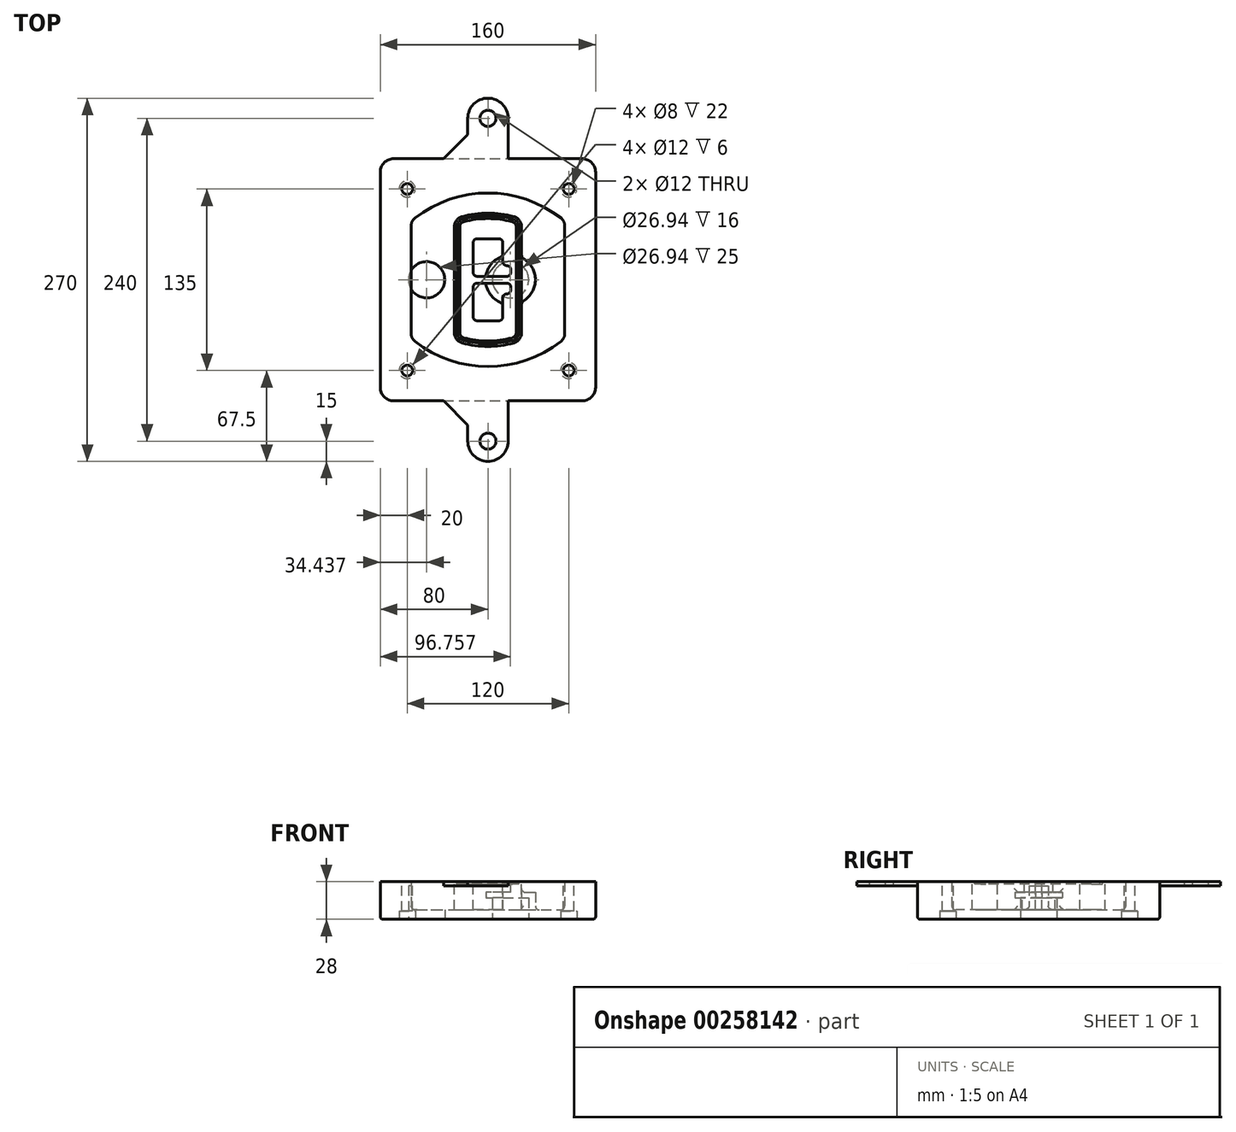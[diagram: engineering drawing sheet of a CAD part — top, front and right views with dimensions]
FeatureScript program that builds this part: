
annotation { "Feature Type Name" : "Feature", "Feature Type Description" : "" }
export const myFeature = defineFeature(function(context is Context, id is Id, definition is map)
    precondition{}
    {
        {
            var Q0;
            Q0=qCreatedBy(makeId("Top.planeOp"),FACE);
            var sketch = newSketch(context, id + "F0", { "sketchPlane" : qUnion([Q0])});
            skPoint(sketch, "E0.rect.middle", {"position": v(0, 0) * mm});
            skLineSegment(sketch, "E1.bottom", {"start": v(-70, -90) * mm, "end": v(70, -90) * mm});
            skLineSegment(sketch, "E1.top", {"start": v(-70, 90) * mm, "end": v(70, 90) * mm});
            skLineSegment(sketch, "E1.left", {"start": v(-80, -80) * mm, "end": v(-80, 80) * mm});
            skLineSegment(sketch, "E1.right", {"start": v(80, -80) * mm, "end": v(80, 80) * mm});
            skLineSegment(sketch, "E2", {"start": v(-80, 90) * mm, "end": v(80, -90) * mm, "construction": true});
            skLineSegment(sketch, "E3", {"start": v(80, 90) * mm, "end": v(-80, -90) * mm, "construction": true});
            skCircle(sketch, "E4", {"center": v(-60, 67.5) * mm, "radius": 4 * mm});
            skCircle(sketch, "E5", {"center": v(60, 67.5) * mm, "radius": 4 * mm});
            skCircle(sketch, "E6", {"center": v(60, -67.5) * mm, "radius": 4 * mm});
            skCircle(sketch, "E7", {"center": v(-60, -67.5) * mm, "radius": 4 * mm});
            skLineSegment(sketch, "E8", {"start": v(-60, 67.5) * mm, "end": v(60, 67.5) * mm, "construction": true});
            skLineSegment(sketch, "E9", {"start": v(60, 67.5) * mm, "end": v(60, -67.5) * mm, "construction": true});
            skLineSegment(sketch, "E10", {"start": v(60, -67.5) * mm, "end": v(-60, -67.5) * mm, "construction": true});
            skLineSegment(sketch, "E11", {"start": v(-60, -67.5) * mm, "end": v(-60, 67.5) * mm, "construction": true});
            skLineSegment(sketch, "E12", {"start": v(-60, 40.3) * mm, "end": v(-60, -40.3) * mm});
            skLineSegment(sketch, "E13", {"start": v(60, 40.3) * mm, "end": v(60, -40.3) * mm});
            skArc(sketch, "E14", {"start": v(56.15, 48.18) * mm, "mid": v(0, 67.5) * mm, "end": v(-56.15, 48.18) * mm});
            skArc(sketch, "E15", {"start": v(-56.15, -48.18) * mm, "mid": v(0, -67.5) * mm, "end": v(56.15, -48.18) * mm});
            skLineSegment(sketch, "E16", {"start": v(-60, 0) * mm, "end": v(60, 0) * mm, "construction": true});
            skPoint(sketch, "E17.visualSharp", {"position": v(-60, -45) * mm});
            skArc(sketch, "E17.filletArc", {"start": v(-60, -40.3) * mm, "mid": v(-58.99, -44.68) * mm, "end": v(-56.15, -48.18) * mm});
            skPoint(sketch, "E18.visualSharp", {"position": v(-60, 45) * mm});
            skArc(sketch, "E18.filletArc", {"start": v(-56.15, 48.18) * mm, "mid": v(-58.99, 44.68) * mm, "end": v(-60, 40.3) * mm});
            skPoint(sketch, "E19.visualSharp", {"position": v(60, 45) * mm});
            skArc(sketch, "E19.filletArc", {"start": v(60, 40.3) * mm, "mid": v(58.99, 44.68) * mm, "end": v(56.15, 48.18) * mm});
            skPoint(sketch, "E20.visualSharp", {"position": v(60, -45) * mm});
            skArc(sketch, "E20.filletArc", {"start": v(56.15, -48.18) * mm, "mid": v(58.99, -44.68) * mm, "end": v(60, -40.3) * mm});
            skPoint(sketch, "E21.visualSharp", {"position": v(-80, 90) * mm});
            skArc(sketch, "E21.filletArc", {"start": v(-70, 90) * mm, "mid": v(-77.07, 87.07) * mm, "end": v(-80, 80) * mm});
            skPoint(sketch, "E22.visualSharp", {"position": v(80, 90) * mm});
            skArc(sketch, "E22.filletArc", {"start": v(80, 80) * mm, "mid": v(77.07, 87.07) * mm, "end": v(70, 90) * mm});
            skPoint(sketch, "E23.visualSharp", {"position": v(80, -90) * mm});
            skArc(sketch, "E23.filletArc", {"start": v(70, -90) * mm, "mid": v(77.07, -87.07) * mm, "end": v(80, -80) * mm});
            skPoint(sketch, "E24.visualSharp", {"position": v(-80, -90) * mm});
            skArc(sketch, "E24.filletArc", {"start": v(-80, -80) * mm, "mid": v(-77.07, -87.07) * mm, "end": v(-70, -90) * mm});
            skArc(sketch, "E25.0", {"start": v(57, 40.3) * mm, "mid": v(56.3, 43.36) * mm, "end": v(54.3, 45.81) * mm});
            skLineSegment(sketch, "E25.1", {"start": v(57, 40.3) * mm, "end": v(57, -40.3) * mm});
            skArc(sketch, "E25.2", {"start": v(54.3, -45.81) * mm, "mid": v(56.3, -43.36) * mm, "end": v(57, -40.3) * mm});
            skArc(sketch, "E25.3", {"start": v(-54.3, -45.81) * mm, "mid": v(0, -64.5) * mm, "end": v(54.3, -45.81) * mm});
            skArc(sketch, "E25.4", {"start": v(-57, -40.3) * mm, "mid": v(-56.3, -43.36) * mm, "end": v(-54.3, -45.81) * mm});
            skArc(sketch, "E25.5", {"start": v(54.3, 45.81) * mm, "mid": v(0, 64.5) * mm, "end": v(-54.3, 45.81) * mm});
            skLineSegment(sketch, "E25.6", {"start": v(-57, 40.3) * mm, "end": v(-57, -40.3) * mm});
            skArc(sketch, "E25.7", {"start": v(-54.3, 45.81) * mm, "mid": v(-56.3, 43.36) * mm, "end": v(-57, 40.3) * mm});
            skArc(sketch, "E26.0", {"start": v(-58.62, 51.33) * mm, "mid": v(-62.58, 46.43) * mm, "end": v(-64, 40.3) * mm});
            skArc(sketch, "E26.1", {"start": v(58.62, 51.33) * mm, "mid": v(0, 71.5) * mm, "end": v(-58.62, 51.33) * mm});
            skArc(sketch, "E26.2", {"start": v(64, 40.3) * mm, "mid": v(62.58, 46.43) * mm, "end": v(58.62, 51.33) * mm});
            skLineSegment(sketch, "E26.3", {"start": v(64, 40.3) * mm, "end": v(64, -40.3) * mm});
            skArc(sketch, "E26.4", {"start": v(58.62, -51.33) * mm, "mid": v(62.58, -46.43) * mm, "end": v(64, -40.3) * mm});
            skLineSegment(sketch, "E26.5", {"start": v(-64, 40.3) * mm, "end": v(-64, -40.3) * mm});
            skArc(sketch, "E26.6", {"start": v(-58.62, -51.33) * mm, "mid": v(0, -71.5) * mm, "end": v(58.62, -51.33) * mm});
            skArc(sketch, "E26.7", {"start": v(-64, -40.3) * mm, "mid": v(-62.58, -46.43) * mm, "end": v(-58.62, -51.33) * mm});
            skSolve(sketch);
        }
        {
            var Q0;
            Q0=makeQuery(id+"F0.imprint","IMPRINT",FACE,{"disambiguationData":[TD([[makeQuery(id+"F0.imprint","IMPRINT",EDGE,{"derivedFrom":sQuery(id+"F0.wireOp",EDGE,"E1.bottom")}),1.0]])]});
            var Q1;
            Q1=makeQuery(id+"F0.imprint","IMPRINT",FACE,{"disambiguationData":[TD([[makeQuery(id+"F0.imprint","IMPRINT",EDGE,{"derivedFrom":sQuery(id+"F0.wireOp",EDGE,"E12")}),1.0]])]});
            var Q2;
            Q2=makeQuery(id+"F0.imprint","IMPRINT",FACE,{"disambiguationData":[TD([[makeQuery(id+"F0.imprint","IMPRINT",EDGE,{"derivedFrom":sQuery(id+"F0.wireOp",EDGE,"E25.0")}),1.0]])]});
            var Q3;
            Q3=makeQuery(id+"F0.imprint","IMPRINT",FACE,{"disambiguationData":[TD([[makeQuery(id+"F0.imprint","IMPRINT",EDGE,{"derivedFrom":sQuery(id+"F0.wireOp",EDGE,"E12")}),-1.0]])]});
            extrude(context, id + "F1", {"entities" : qUnion([Q0, Q1, Q2, Q3]), "oppositeDirection" : true, "depth" : 25 * mm});
        }
        {
            var Q0;
            Q0=makeQuery(id+"F0.imprint","IMPRINT",FACE,{"disambiguationData":[TD([[makeQuery(id+"F0.imprint","IMPRINT",EDGE,{"derivedFrom":sQuery(id+"F0.wireOp",EDGE,"E12")}),1.0]])]});
            extrude(context, id + "F2", {"entities" : qUnion([Q0]), "operationType" : NewBodyOperationType.ADD, "depth" : 3 * mm});
        }
        {
            var Q0;
            Q0=makeQuery(id+"F0.imprint","IMPRINT",FACE,{"disambiguationData":[TD([[makeQuery(id+"F0.imprint","IMPRINT",EDGE,{"derivedFrom":sQuery(id+"F0.wireOp",EDGE,"E25.0")}),1.0]])]});
            extrude(context, id + "F3", {"entities" : qUnion([Q0]), "operationType" : NewBodyOperationType.REMOVE, "oppositeDirection" : true, "depth" : 18 * mm});
        }
        {
            var Q0;
            Q0=makeQuery(id+"F2.opExtrude","CAP_FACE",FACE,{"disambiguationData":[OSD([sQuery(id+"F0.wireOp",EDGE,"E12"),sQuery(id+"F0.wireOp",EDGE,"E13"),sQuery(id+"F0.wireOp",EDGE,"E14"),sQuery(id+"F0.wireOp",EDGE,"E15"),sQuery(id+"F0.wireOp",EDGE,"E17.filletArc"),sQuery(id+"F0.wireOp",EDGE,"E18.filletArc"),sQuery(id+"F0.wireOp",EDGE,"E19.filletArc"),sQuery(id+"F0.wireOp",EDGE,"E20.filletArc"),sQuery(id+"F0.wireOp",EDGE,"E25.0"),sQuery(id+"F0.wireOp",EDGE,"E25.1"),sQuery(id+"F0.wireOp",EDGE,"E25.2"),sQuery(id+"F0.wireOp",EDGE,"E25.3"),sQuery(id+"F0.wireOp",EDGE,"E25.4"),sQuery(id+"F0.wireOp",EDGE,"E25.5"),sQuery(id+"F0.wireOp",EDGE,"E25.6"),sQuery(id+"F0.wireOp",EDGE,"E25.7")])],"isStart":false});
            var sketch = newSketch(context, id + "F4", { "sketchPlane" : qUnion([Q0])});
            skArc(sketch, "E27.0", {"start": v(-19.08, -46.97) * mm, "mid": v(0, -49.5) * mm, "end": v(19.08, -46.97) * mm});
            skArc(sketch, "E28.0", {"start": v(19.08, 46.97) * mm, "mid": v(0, 49.5) * mm, "end": v(-19.08, 46.97) * mm});
            skLineSegment(sketch, "E29", {"start": v(-25, 39.25) * mm, "end": v(-25, -39.25) * mm});
            skLineSegment(sketch, "E30", {"start": v(25, 39.25) * mm, "end": v(25, -39.25) * mm});
            skLineSegment(sketch, "E31", {"start": v(-25, 45.1) * mm, "end": v(25, 45.1) * mm, "construction": true});
            skLineSegment(sketch, "E32", {"start": v(-25, -45.1) * mm, "end": v(25, -45.1) * mm, "construction": true});
            skPoint(sketch, "E33.visualSharp", {"position": v(-25, 45.1) * mm});
            skArc(sketch, "E33.filletArc", {"start": v(-19.08, 46.97) * mm, "mid": v(-23.35, 44.11) * mm, "end": v(-25, 39.25) * mm});
            skPoint(sketch, "E34.visualSharp", {"position": v(25, 45.1) * mm});
            skArc(sketch, "E34.filletArc", {"start": v(25, 39.25) * mm, "mid": v(23.35, 44.11) * mm, "end": v(19.08, 46.97) * mm});
            skPoint(sketch, "E35.visualSharp", {"position": v(25, -45.1) * mm});
            skArc(sketch, "E35.filletArc", {"start": v(19.08, -46.97) * mm, "mid": v(23.35, -44.11) * mm, "end": v(25, -39.25) * mm});
            skPoint(sketch, "E36.visualSharp", {"position": v(-25, -45.1) * mm});
            skArc(sketch, "E36.filletArc", {"start": v(-25, -39.25) * mm, "mid": v(-23.35, -44.11) * mm, "end": v(-19.08, -46.97) * mm});
            skArc(sketch, "E37.0", {"start": v(54.3, 45.81) * mm, "mid": v(0, 64.5) * mm, "end": v(-54.3, 45.81) * mm});
            skArc(sketch, "E37.1", {"start": v(-54.3, 45.81) * mm, "mid": v(-56.3, 43.36) * mm, "end": v(-57, 40.3) * mm});
            skLineSegment(sketch, "E37.2", {"start": v(-57, 40.3) * mm, "end": v(-57, -40.3) * mm});
            skArc(sketch, "E37.3", {"start": v(-57, -40.3) * mm, "mid": v(-56.3, -43.36) * mm, "end": v(-54.3, -45.81) * mm});
            skArc(sketch, "E37.4", {"start": v(-54.3, -45.81) * mm, "mid": v(0, -64.5) * mm, "end": v(54.3, -45.81) * mm});
            skArc(sketch, "E37.5", {"start": v(54.3, -45.81) * mm, "mid": v(56.3, -43.36) * mm, "end": v(57, -40.3) * mm});
            skLineSegment(sketch, "E37.6", {"start": v(57, 40.3) * mm, "end": v(57, -40.3) * mm});
            skArc(sketch, "E37.7", {"start": v(57, 40.3) * mm, "mid": v(56.3, 43.36) * mm, "end": v(54.3, 45.81) * mm});
            skLineSegment(sketch, "E38.0", {"start": v(23, 39.25) * mm, "end": v(23, -39.25) * mm});
            skArc(sketch, "E38.1", {"start": v(18.56, -45.04) * mm, "mid": v(21.76, -42.9) * mm, "end": v(23, -39.25) * mm});
            skArc(sketch, "E38.2", {"start": v(-18.56, -45.04) * mm, "mid": v(0, -47.5) * mm, "end": v(18.56, -45.04) * mm});
            skArc(sketch, "E38.3", {"start": v(-23, -39.25) * mm, "mid": v(-21.76, -42.9) * mm, "end": v(-18.56, -45.04) * mm});
            skLineSegment(sketch, "E38.4", {"start": v(-23, 39.25) * mm, "end": v(-23, -39.25) * mm});
            skArc(sketch, "E38.5", {"start": v(23, 39.25) * mm, "mid": v(21.76, 42.9) * mm, "end": v(18.56, 45.04) * mm});
            skArc(sketch, "E38.6", {"start": v(-18.56, 45.04) * mm, "mid": v(-21.76, 42.9) * mm, "end": v(-23, 39.25) * mm});
            skArc(sketch, "E38.7", {"start": v(18.56, 45.04) * mm, "mid": v(0, 47.5) * mm, "end": v(-18.56, 45.04) * mm});
            skArc(sketch, "E39.0", {"start": v(21, 39.25) * mm, "mid": v(20.18, 41.68) * mm, "end": v(18.04, 43.1) * mm});
            skLineSegment(sketch, "E39.1", {"start": v(21, 39.25) * mm, "end": v(21, -39.25) * mm});
            skArc(sketch, "E39.2", {"start": v(18.04, -43.1) * mm, "mid": v(20.18, -41.68) * mm, "end": v(21, -39.25) * mm});
            skArc(sketch, "E39.3", {"start": v(-18.04, -43.1) * mm, "mid": v(0, -45.5) * mm, "end": v(18.04, -43.1) * mm});
            skArc(sketch, "E39.4", {"start": v(-21, -39.25) * mm, "mid": v(-20.18, -41.68) * mm, "end": v(-18.04, -43.1) * mm});
            skArc(sketch, "E39.5", {"start": v(18.04, 43.1) * mm, "mid": v(0, 45.5) * mm, "end": v(-18.04, 43.1) * mm});
            skLineSegment(sketch, "E39.6", {"start": v(-21, 39.25) * mm, "end": v(-21, -39.25) * mm});
            skArc(sketch, "E39.7", {"start": v(-18.04, 43.1) * mm, "mid": v(-20.18, 41.68) * mm, "end": v(-21, 39.25) * mm});
            skLineSegment(sketch, "E40", {"start": v(-25, 0) * mm, "end": v(25, 0) * mm, "construction": true});
            skLineSegment(sketch, "E41", {"start": v(-11, 5.5) * mm, "end": v(-11, 27.5) * mm});
            skLineSegment(sketch, "E42", {"start": v(-8, 30.5) * mm, "end": v(8, 30.5) * mm});
            skLineSegment(sketch, "E43", {"start": v(11, 27.5) * mm, "end": v(11, 13.5) * mm});
            skLineSegment(sketch, "E44", {"start": v(14, 10.5) * mm, "end": v(14, 10.5) * mm});
            skLineSegment(sketch, "E45", {"start": v(17, 7.5) * mm, "end": v(17, 5.5) * mm});
            skLineSegment(sketch, "E46", {"start": v(14, 2.5) * mm, "end": v(-8, 2.5) * mm});
            skPoint(sketch, "E47.visualSharp", {"position": v(-11, 30.5) * mm});
            skArc(sketch, "E47.filletArc", {"start": v(-8, 30.5) * mm, "mid": v(-10.12, 29.62) * mm, "end": v(-11, 27.5) * mm});
            skPoint(sketch, "E48.visualSharp", {"position": v(11, 30.5) * mm});
            skArc(sketch, "E48.filletArc", {"start": v(11, 27.5) * mm, "mid": v(10.12, 29.62) * mm, "end": v(8, 30.5) * mm});
            skPoint(sketch, "E49.visualSharp", {"position": v(11, 10.5) * mm});
            skArc(sketch, "E49.filletArc", {"start": v(11, 13.5) * mm, "mid": v(11.88, 11.38) * mm, "end": v(14, 10.5) * mm});
            skPoint(sketch, "E50.visualSharp", {"position": v(17, 10.5) * mm});
            skArc(sketch, "E50.filletArc", {"start": v(17, 7.5) * mm, "mid": v(16.12, 9.62) * mm, "end": v(14, 10.5) * mm});
            skPoint(sketch, "E51.visualSharp", {"position": v(17, 2.5) * mm});
            skArc(sketch, "E51.filletArc", {"start": v(14, 2.5) * mm, "mid": v(16.12, 3.38) * mm, "end": v(17, 5.5) * mm});
            skPoint(sketch, "E52.visualSharp", {"position": v(-11, 2.5) * mm});
            skArc(sketch, "E52.filletArc", {"start": v(-11, 5.5) * mm, "mid": v(-10.12, 3.38) * mm, "end": v(-8, 2.5) * mm});
            skLineSegment(sketch, "E53.0.MirrorCS", {"start": v(14, -2.5) * mm, "end": v(-8, -2.5) * mm});
            skArc(sketch, "E54.0.MirrorCS", {"start": v(-11, -5.5) * mm, "mid": v(-10.12, -3.38) * mm, "end": v(-8, -2.5) * mm});
            skLineSegment(sketch, "E55.0.MirrorCS", {"start": v(-11, -5.5) * mm, "end": v(-11, -27.5) * mm});
            skArc(sketch, "E56.0.MirrorCS", {"start": v(-8, -30.5) * mm, "mid": v(-10.12, -29.62) * mm, "end": v(-11, -27.5) * mm});
            skLineSegment(sketch, "E57.0.MirrorCS", {"start": v(-8, -30.5) * mm, "end": v(8, -30.5) * mm});
            skArc(sketch, "E58.0.MirrorCS", {"start": v(11, -27.5) * mm, "mid": v(10.12, -29.62) * mm, "end": v(8, -30.5) * mm});
            skLineSegment(sketch, "E59.0.MirrorCS", {"start": v(11, -27.5) * mm, "end": v(11, -13.5) * mm});
            skArc(sketch, "E60.0.MirrorCS", {"start": v(11, -13.5) * mm, "mid": v(11.88, -11.38) * mm, "end": v(14, -10.5) * mm});
            skArc(sketch, "E61.0.MirrorCS", {"start": v(17, -7.5) * mm, "mid": v(16.12, -9.62) * mm, "end": v(14, -10.5) * mm});
            skLineSegment(sketch, "E62.0.MirrorCS", {"start": v(17, -7.5) * mm, "end": v(17, -5.5) * mm});
            skArc(sketch, "E63.0.MirrorCS", {"start": v(14, -2.5) * mm, "mid": v(16.12, -3.38) * mm, "end": v(17, -5.5) * mm});
            skSolve(sketch);
        }
        {
            var Q0;
            Q0=makeQuery(id+"F4.imprint","IMPRINT",FACE,{"disambiguationData":[TD([[makeQuery(id+"F4.imprint","IMPRINT",EDGE,{"derivedFrom":sQuery(id+"F4.wireOp",EDGE,"E27.0")}),1.0]])]});
            var Q1;
            Q1=makeQuery(id+"F4.imprint","IMPRINT",FACE,{"disambiguationData":[TD([[makeQuery(id+"F4.imprint","IMPRINT",EDGE,{"derivedFrom":sQuery(id+"F4.wireOp",EDGE,"E38.0")}),-1.0]])]});
            var Q2;
            Q2=makeQuery(id+"F4.imprint","IMPRINT",FACE,{"disambiguationData":[TD([[makeQuery(id+"F4.imprint","IMPRINT",EDGE,{"derivedFrom":sQuery(id+"F4.wireOp",EDGE,"E39.0")}),1.0]])]});
            extrude(context, id + "F5", {"entities" : qUnion([Q0, Q1, Q2]), "operationType" : NewBodyOperationType.ADD, "endBound" : BoundingType.UP_TO_NEXT, "oppositeDirection" : true, "depth" : 25 * mm});
        }
        {
            var Q0;
            Q0=makeQuery(id+"F4.imprint","IMPRINT",FACE,{"disambiguationData":[TD([[makeQuery(id+"F4.imprint","IMPRINT",EDGE,{"derivedFrom":sQuery(id+"F4.wireOp",EDGE,"E38.0")}),-1.0]])]});
            extrude(context, id + "F6", {"entities" : qUnion([Q0]), "operationType" : NewBodyOperationType.REMOVE, "oppositeDirection" : true, "depth" : 2 * mm});
        }
        {
            var Q0;
            Q0=makeQuery(id+"F1.opExtrude","CAP_FACE",FACE,{"disambiguationData":[OSD([sQuery(id+"F0.wireOp",EDGE,"E1.bottom"),sQuery(id+"F0.wireOp",EDGE,"E1.top"),sQuery(id+"F0.wireOp",EDGE,"E1.left"),sQuery(id+"F0.wireOp",EDGE,"E1.right"),sQuery(id+"F0.wireOp",EDGE,"E4"),sQuery(id+"F0.wireOp",EDGE,"E5"),sQuery(id+"F0.wireOp",EDGE,"E6"),sQuery(id+"F0.wireOp",EDGE,"E7"),sQuery(id+"F0.wireOp",EDGE,"E21.filletArc"),sQuery(id+"F0.wireOp",EDGE,"E22.filletArc"),sQuery(id+"F0.wireOp",EDGE,"E23.filletArc"),sQuery(id+"F0.wireOp",EDGE,"E24.filletArc")])],"isStart":false});
            var sketch = newSketch(context, id + "F7", { "sketchPlane" : qUnion([Q0])});
            skCircle(sketch, "E64", {"center": v(16.76, 0) * mm, "radius": 13.47 * mm});
            skCircle(sketch, "E65", {"center": v(-45.56, 0) * mm, "radius": 13.47 * mm});
            skLineSegment(sketch, "E66", {"start": v(80, 0) * mm, "end": v(-80, 0) * mm});
            skCircle(sketch, "E67", {"center": v(16.76, 0) * mm, "radius": 18.47 * mm});
            skCircle(sketch, "E68", {"center": v(60, -67.5) * mm, "radius": 6 * mm});
            skCircle(sketch, "E69", {"center": v(-60, -67.5) * mm, "radius": 6 * mm});
            skCircle(sketch, "E70", {"center": v(-60, 67.5) * mm, "radius": 6 * mm});
            skCircle(sketch, "E71", {"center": v(60, 67.5) * mm, "radius": 6 * mm});
            skSolve(sketch);
        }
        {
            var Q0;
            {var subQ1=sQuery(id+"F7.wireOp",EDGE,"E66");var subQ4=sQuery(id+"F7.wireOp",EDGE,"E64");var subQ6=makeQuery(id+"F7.imprint","INTERSECT",VERTEX,{"disambiguationData":[OD(0.0)],"derivedFrom":[subQ4,subQ1]});Q0=makeQuery(id+"F7.imprint","IMPRINT",FACE,{"disambiguationData":[TD([[makeQuery(id+"F7.imprint","IMPRINT",EDGE,{"disambiguationData":[TD([[subQ6,-1.0]])],"derivedFrom":subQ4}),-1.0]])]});}
            var Q1;
            {var subQ0=sQuery(id+"F7.wireOp",EDGE,"E66");var subQ1=sQuery(id+"F7.wireOp",EDGE,"E64");var subQ3=makeQuery(id+"F7.imprint","INTERSECT",VERTEX,{"disambiguationData":[OD(0.0)],"derivedFrom":[subQ1,subQ0]});Q1=makeQuery(id+"F7.imprint","IMPRINT",FACE,{"disambiguationData":[TD([[makeQuery(id+"F7.imprint","IMPRINT",EDGE,{"disambiguationData":[TD([[subQ3,-1.0]])],"derivedFrom":subQ1}),1.0]])]});}
            var Q2;
            {var subQ0=sQuery(id+"F7.wireOp",EDGE,"E66");var subQ1=sQuery(id+"F7.wireOp",EDGE,"E64");var subQ3=makeQuery(id+"F7.imprint","INTERSECT",VERTEX,{"disambiguationData":[OD(0.0)],"derivedFrom":[subQ1,subQ0]});Q2=makeQuery(id+"F7.imprint","IMPRINT",FACE,{"disambiguationData":[TD([[makeQuery(id+"F7.imprint","IMPRINT",EDGE,{"disambiguationData":[TD([[subQ3,1.0]])],"derivedFrom":subQ1}),1.0]])]});}
            var Q3;
            {var subQ1=sQuery(id+"F7.wireOp",EDGE,"E66");var subQ4=sQuery(id+"F7.wireOp",EDGE,"E64");var subQ6=makeQuery(id+"F7.imprint","INTERSECT",VERTEX,{"disambiguationData":[OD(0.0)],"derivedFrom":[subQ4,subQ1]});Q3=makeQuery(id+"F7.imprint","IMPRINT",FACE,{"disambiguationData":[TD([[makeQuery(id+"F7.imprint","IMPRINT",EDGE,{"disambiguationData":[TD([[subQ6,1.0]])],"derivedFrom":subQ4}),-1.0]])]});}
            extrude(context, id + "F8", {"entities" : qUnion([Q0, Q1, Q2, Q3]), "operationType" : NewBodyOperationType.ADD, "oppositeDirection" : true, "depth" : 20 * mm});
        }
        {
            var Q0;
            {var subQ0=sQuery(id+"F7.wireOp",EDGE,"E66");var subQ1=sQuery(id+"F7.wireOp",EDGE,"E64");var subQ3=makeQuery(id+"F7.imprint","INTERSECT",VERTEX,{"disambiguationData":[OD(0.0)],"derivedFrom":[subQ1,subQ0]});Q0=makeQuery(id+"F7.imprint","IMPRINT",FACE,{"disambiguationData":[TD([[makeQuery(id+"F7.imprint","IMPRINT",EDGE,{"disambiguationData":[TD([[subQ3,-1.0]])],"derivedFrom":subQ1}),1.0]])]});}
            var Q1;
            {var subQ0=sQuery(id+"F7.wireOp",EDGE,"E66");var subQ1=sQuery(id+"F7.wireOp",EDGE,"E64");var subQ3=makeQuery(id+"F7.imprint","INTERSECT",VERTEX,{"disambiguationData":[OD(0.0)],"derivedFrom":[subQ1,subQ0]});Q1=makeQuery(id+"F7.imprint","IMPRINT",FACE,{"disambiguationData":[TD([[makeQuery(id+"F7.imprint","IMPRINT",EDGE,{"disambiguationData":[TD([[subQ3,1.0]])],"derivedFrom":subQ1}),1.0]])]});}
            extrude(context, id + "F9", {"entities" : qUnion([Q0, Q1]), "operationType" : NewBodyOperationType.REMOVE, "oppositeDirection" : true, "depth" : 16 * mm});
        }
        {
            var Q0;
            {var subQ0=sQuery(id+"F7.wireOp",EDGE,"E66");var subQ1=sQuery(id+"F7.wireOp",EDGE,"E65");var subQ3=makeQuery(id+"F7.imprint","INTERSECT",VERTEX,{"disambiguationData":[OD(0.0)],"derivedFrom":[subQ1,subQ0]});Q0=makeQuery(id+"F7.imprint","IMPRINT",FACE,{"disambiguationData":[TD([[makeQuery(id+"F7.imprint","IMPRINT",EDGE,{"disambiguationData":[TD([[subQ3,-1.0]])],"derivedFrom":subQ1}),1.0]])]});}
            var Q1;
            {var subQ0=sQuery(id+"F7.wireOp",EDGE,"E66");var subQ1=sQuery(id+"F7.wireOp",EDGE,"E65");var subQ3=makeQuery(id+"F7.imprint","INTERSECT",VERTEX,{"disambiguationData":[OD(0.0)],"derivedFrom":[subQ1,subQ0]});Q1=makeQuery(id+"F7.imprint","IMPRINT",FACE,{"disambiguationData":[TD([[makeQuery(id+"F7.imprint","IMPRINT",EDGE,{"disambiguationData":[TD([[subQ3,1.0]])],"derivedFrom":subQ1}),1.0]])]});}
            extrude(context, id + "F10", {"entities" : qUnion([Q0, Q1]), "operationType" : NewBodyOperationType.REMOVE, "oppositeDirection" : true, "depth" : 25 * mm});
        }
        {
            var Q0;
            Q0=makeQuery(id+"F7.imprint","IMPRINT",FACE,{"disambiguationData":[TD([[makeQuery(id+"F7.imprint","IMPRINT",EDGE,{"derivedFrom":sQuery(id+"F7.wireOp",EDGE,"E68")}),1.0]])]});
            var Q1;
            Q1=makeQuery(id+"F7.imprint","IMPRINT",FACE,{"disambiguationData":[TD([[makeQuery(id+"F7.imprint","IMPRINT",EDGE,{"derivedFrom":makeQuery(id+"F1.opExtrude","CAP_EDGE",EDGE,{"disambiguationData":[OSD([sQuery(id+"F0.wireOp",EDGE,"E5")])],"isStart":false})}),-1.0]])]});
            var Q2;
            Q2=makeQuery(id+"F7.imprint","IMPRINT",FACE,{"disambiguationData":[TD([[makeQuery(id+"F7.imprint","IMPRINT",EDGE,{"derivedFrom":sQuery(id+"F7.wireOp",EDGE,"E69")}),1.0]])]});
            var Q3;
            Q3=makeQuery(id+"F7.imprint","IMPRINT",FACE,{"disambiguationData":[TD([[makeQuery(id+"F7.imprint","IMPRINT",EDGE,{"derivedFrom":makeQuery(id+"F1.opExtrude","CAP_EDGE",EDGE,{"disambiguationData":[OSD([sQuery(id+"F0.wireOp",EDGE,"E4")])],"isStart":false})}),-1.0]])]});
            var Q4;
            Q4=makeQuery(id+"F7.imprint","IMPRINT",FACE,{"disambiguationData":[TD([[makeQuery(id+"F7.imprint","IMPRINT",EDGE,{"derivedFrom":sQuery(id+"F7.wireOp",EDGE,"E70")}),1.0]])]});
            var Q5;
            Q5=makeQuery(id+"F7.imprint","IMPRINT",FACE,{"disambiguationData":[TD([[makeQuery(id+"F7.imprint","IMPRINT",EDGE,{"derivedFrom":makeQuery(id+"F1.opExtrude","CAP_EDGE",EDGE,{"disambiguationData":[OSD([sQuery(id+"F0.wireOp",EDGE,"E7")])],"isStart":false})}),-1.0]])]});
            var Q6;
            Q6=makeQuery(id+"F7.imprint","IMPRINT",FACE,{"disambiguationData":[TD([[makeQuery(id+"F7.imprint","IMPRINT",EDGE,{"derivedFrom":sQuery(id+"F7.wireOp",EDGE,"E71")}),1.0]])]});
            var Q7;
            Q7=makeQuery(id+"F7.imprint","IMPRINT",FACE,{"disambiguationData":[TD([[makeQuery(id+"F7.imprint","IMPRINT",EDGE,{"derivedFrom":makeQuery(id+"F1.opExtrude","CAP_EDGE",EDGE,{"disambiguationData":[OSD([sQuery(id+"F0.wireOp",EDGE,"E6")])],"isStart":false})}),-1.0]])]});
            extrude(context, id + "F11", {"entities" : qUnion([Q0, Q1, Q2, Q3, Q4, Q5, Q6, Q7]), "operationType" : NewBodyOperationType.REMOVE, "oppositeDirection" : true, "depth" : 6 * mm});
        }
        {
            var Q0;
            Q0=makeQuery(id+"F9.boolean.opBoolean","COPY",FACE,{"derivedFrom":makeQuery(id+"F9.opExtrude","CAP_FACE",FACE,{"disambiguationData":[OSD([sQuery(id+"F7.wireOp",EDGE,"E64")])],"isStart":false})});
            var sketch = newSketch(context, id + "F12", { "sketchPlane" : qUnion([Q0])});
            skArc(sketch, "E72.0", {"start": v(11, 17.55) * mm, "mid": v(2.57, 11.82) * mm, "end": v(-1.54, 2.5) * mm});
            skArc(sketch, "E72.1", {"start": v(-1.54, -2.5) * mm, "mid": v(2.57, -11.82) * mm, "end": v(11, -17.55) * mm});
            skLineSegment(sketch, "E73", {"start": v(-1.54, -2.5) * mm, "end": v(14, -2.5) * mm});
            skLineSegment(sketch, "E74.0", {"start": v(14, 2.5) * mm, "end": v(-1.54, 2.5) * mm});
            skArc(sketch, "E74.1", {"start": v(14, 2.5) * mm, "mid": v(16.12, 3.38) * mm, "end": v(17, 5.5) * mm});
            skLineSegment(sketch, "E74.2", {"start": v(17, 7.5) * mm, "end": v(17, 5.5) * mm});
            skArc(sketch, "E74.3", {"start": v(17, 7.5) * mm, "mid": v(16.12, 9.62) * mm, "end": v(14, 10.5) * mm});
            skArc(sketch, "E74.4", {"start": v(11, 13.5) * mm, "mid": v(11.88, 11.38) * mm, "end": v(14, 10.5) * mm});
            skLineSegment(sketch, "E74.5", {"start": v(11, 17.55) * mm, "end": v(11, 13.5) * mm});
            skLineSegment(sketch, "E74.7", {"start": v(14, -2.5) * mm, "end": v(-1.54, -2.5) * mm});
            skArc(sketch, "E74.8", {"start": v(14, -2.5) * mm, "mid": v(16.12, -3.38) * mm, "end": v(17, -5.5) * mm});
            skLineSegment(sketch, "E74.9", {"start": v(17, -7.5) * mm, "end": v(17, -5.5) * mm});
            skArc(sketch, "E74.10", {"start": v(17, -7.5) * mm, "mid": v(16.12, -9.62) * mm, "end": v(14, -10.5) * mm});
            skArc(sketch, "E74.11", {"start": v(11, -13.5) * mm, "mid": v(11.88, -11.38) * mm, "end": v(14, -10.5) * mm});
            skLineSegment(sketch, "E74.12", {"start": v(11, -17.55) * mm, "end": v(11, -13.5) * mm});
            skPoint(sketch, "E75.orphan", {"position": v(11, -27.5) * mm});
            skPoint(sketch, "E76.orphan", {"position": v(-8, -2.5) * mm});
            skPoint(sketch, "E77.orphan", {"position": v(-8, 2.5) * mm});
            skPoint(sketch, "E78.orphan", {"position": v(11, 27.5) * mm});
            skSolve(sketch);
        }
        {
            var Q0;
            {var subQ7=sQuery(id+"F12.wireOp",EDGE,"E72.0");var subQ14=sQuery(id+"F12.wireOp",EDGE,"E72.1");var subQ16=sQuery(id+"F12.wireOp",EDGE,"E74.1");var subQ18=sQuery(id+"F12.wireOp",EDGE,"E74.8");Q0=qUnion([makeQuery(id+"F12.imprint","IMPRINT",FACE,{"disambiguationData":[TD([[makeQuery(id+"F12.imprint","IMPRINT",EDGE,{"derivedFrom":subQ7}),1.0]])]}),makeQuery(id+"F12.imprint","IMPRINT",FACE,{"disambiguationData":[TD([[makeQuery(id+"F12.imprint","IMPRINT",EDGE,{"derivedFrom":subQ14}),1.0]])]}),makeQuery(id+"F12.imprint","IMPRINT",FACE,{"disambiguationData":[TD([[makeQuery(id+"F12.imprint","IMPRINT",EDGE,{"derivedFrom":subQ16}),1.0]])]}),makeQuery(id+"F12.imprint","IMPRINT",FACE,{"disambiguationData":[TD([[makeQuery(id+"F12.imprint","IMPRINT",EDGE,{"derivedFrom":subQ18}),-1.0]])]})]);}
            var Q1;
            Q1=makeQuery(id+"F5.boolean.opBoolean","SPLIT",FACE,{"disambiguationData":[TD([makeQuery(id+"F5.opExtrude","SWEPT_FACE",FACE,{"disambiguationData":[OSD([sQuery(id+"F4.wireOp",EDGE,"E41")])]})])],"derivedFrom":makeQuery(id+"F3.boolean.opBoolean","COPY",FACE,{"derivedFrom":makeQuery(id+"F3.opExtrude","CAP_FACE",FACE,{"disambiguationData":[OSD([sQuery(id+"F0.wireOp",EDGE,"E25.0"),sQuery(id+"F0.wireOp",EDGE,"E25.1"),sQuery(id+"F0.wireOp",EDGE,"E25.2"),sQuery(id+"F0.wireOp",EDGE,"E25.3"),sQuery(id+"F0.wireOp",EDGE,"E25.4"),sQuery(id+"F0.wireOp",EDGE,"E25.5"),sQuery(id+"F0.wireOp",EDGE,"E25.6"),sQuery(id+"F0.wireOp",EDGE,"E25.7")])],"isStart":false})})});
            extrude(context, id + "F13", {"entities" : qUnion([Q0]), "operationType" : NewBodyOperationType.REMOVE, "endBound" : BoundingType.UP_TO_SURFACE, "endBoundEntityFace" : qUnion([Q1]), "depth" : 25 * mm});
        }
        {
            var Q0;
            Q0=makeQuery(id+"F3.boolean.opBoolean","COPY",EDGE,{"derivedFrom":makeQuery(id+"F3.opExtrude","CAP_EDGE",EDGE,{"disambiguationData":[OSD([sQuery(id+"F0.wireOp",EDGE,"E25.6")])],"isStart":false})});
            var Q1;
            Q1=makeQuery(id+"F8.boolean.opBoolean","INTERSECT",EDGE,{"derivedFrom":[makeQuery(id+"F5.opExtrude","SWEPT_FACE",FACE,{"disambiguationData":[OSD([sQuery(id+"F4.wireOp",EDGE,"E30")])]}),makeQuery(id+"F8.opExtrude","CAP_FACE",FACE,{"disambiguationData":[OSD([sQuery(id+"F7.wireOp",EDGE,"E67")])],"isStart":false})]});
            var Q2;
            Q2=makeQuery(id+"F8.boolean.opBoolean","INTERSECT",EDGE,{"disambiguationData":[OD(1.0)],"derivedFrom":[makeQuery(id+"F5.opExtrude","SWEPT_FACE",FACE,{"disambiguationData":[OSD([sQuery(id+"F4.wireOp",EDGE,"E30")])]}),makeQuery(id+"F8.opExtrude","SWEPT_FACE",FACE,{"disambiguationData":[OSD([sQuery(id+"F7.wireOp",EDGE,"E67")])]})]});
            var Q3;
            {var subQ0=sQuery(id+"F4.wireOp",EDGE,"E30");Q3=makeQuery(id+"F8.boolean.opBoolean","SPLIT",EDGE,{"disambiguationData":[TD([makeQuery(id+"F5.opExtrude","SWEPT_FACE",FACE,{"disambiguationData":[OSD([sQuery(id+"F4.wireOp",EDGE,"E35.filletArc")])]})])],"derivedFrom":makeQuery(id+"F5.opExtrude","CAP_EDGE",EDGE,{"disambiguationData":[OSD([subQ0])],"isStart":false})});}
            var Q4;
            {var subQ0=sQuery(id+"F0.wireOp",EDGE,"E25.7");var subQ1=sQuery(id+"F0.wireOp",EDGE,"E25.1");var subQ2=sQuery(id+"F0.wireOp",EDGE,"E25.6");var subQ3=sQuery(id+"F0.wireOp",EDGE,"E25.5");var subQ4=sQuery(id+"F0.wireOp",EDGE,"E25.4");var subQ5=sQuery(id+"F0.wireOp",EDGE,"E25.0");var subQ6=sQuery(id+"F0.wireOp",EDGE,"E25.2");var subQ7=sQuery(id+"F0.wireOp",EDGE,"E25.3");Q4=makeQuery(id+"F8.boolean.opBoolean","INTERSECT",EDGE,{"derivedFrom":[makeQuery(id+"F5.boolean.opBoolean","SPLIT",FACE,{"disambiguationData":[TD([makeQuery(id+"F2.opExtrude","SWEPT_FACE",FACE,{"disambiguationData":[OSD([subQ5])]})])],"derivedFrom":makeQuery(id+"F3.boolean.opBoolean","COPY",FACE,{"derivedFrom":makeQuery(id+"F3.opExtrude","CAP_FACE",FACE,{"disambiguationData":[OSD([subQ5,subQ1,subQ6,subQ7,subQ4,subQ3,subQ2,subQ0])],"isStart":false})})}),makeQuery(id+"F8.opExtrude","SWEPT_FACE",FACE,{"disambiguationData":[OSD([sQuery(id+"F7.wireOp",EDGE,"E67")])]})]});}
            var Q5;
            Q5=makeQuery(id+"F8.boolean.opBoolean","INTERSECT",EDGE,{"disambiguationData":[OD(0.0)],"derivedFrom":[makeQuery(id+"F5.opExtrude","SWEPT_FACE",FACE,{"disambiguationData":[OSD([sQuery(id+"F4.wireOp",EDGE,"E30")])]}),makeQuery(id+"F8.opExtrude","SWEPT_FACE",FACE,{"disambiguationData":[OSD([sQuery(id+"F7.wireOp",EDGE,"E67")])]})]});
            fillet(context, id + "F14", {"entities" : qUnion([Q0, Q1, Q2, Q3, Q4, Q5]), "radius" : 3 * mm, "tangentPropagation" : true, "allowEdgeOverflow" : false});
        }
        {
            var Q0;
            Q0=makeQuery(id+"F1.opExtrude","CAP_EDGE",EDGE,{"disambiguationData":[OSD([sQuery(id+"F0.wireOp",EDGE,"E1.bottom")])],"isStart":false});
            fillet(context, id + "F15", {"entities" : qUnion([Q0]), "radius" : 2 * mm, "tangentPropagation" : true, "allowEdgeOverflow" : false});
        }
        {
            var Q0;
            {var subQ0=sQuery(id+"F0.wireOp",EDGE,"E22.filletArc");var subQ1=sQuery(id+"F0.wireOp",EDGE,"E7");var subQ2=sQuery(id+"F0.wireOp",EDGE,"E6");var subQ3=sQuery(id+"F0.wireOp",EDGE,"E5");var subQ4=sQuery(id+"F0.wireOp",EDGE,"E4");var subQ5=sQuery(id+"F0.wireOp",EDGE,"E1.bottom");var subQ6=sQuery(id+"F0.wireOp",EDGE,"E21.filletArc");var subQ7=sQuery(id+"F0.wireOp",EDGE,"E1.top");var subQ8=sQuery(id+"F0.wireOp",EDGE,"E1.left");var subQ9=sQuery(id+"F0.wireOp",EDGE,"E1.right");var subQ10=sQuery(id+"F0.wireOp",EDGE,"E23.filletArc");var subQ11=sQuery(id+"F0.wireOp",EDGE,"E24.filletArc");Q0=makeQuery(id+"F2.boolean.opBoolean","SPLIT",FACE,{"disambiguationData":[TD([makeQuery(id+"F1.opExtrude","SWEPT_FACE",FACE,{"disambiguationData":[OSD([subQ5])]})])],"derivedFrom":makeQuery(id+"F1.opExtrude","CAP_FACE",FACE,{"disambiguationData":[OSD([subQ5,subQ7,subQ8,subQ9,subQ4,subQ3,subQ2,subQ1,subQ6,subQ0,subQ10,subQ11])],"isStart":true})});}
            var sketch = newSketch(context, id + "F16", { "sketchPlane" : qUnion([Q0])});
            skCircle(sketch, "E79", {"center": v(0, 120) * mm, "radius": 6 * mm});
            skLineSegment(sketch, "E80", {"start": v(0, 120) * mm, "end": v(0, 90) * mm, "construction": true});
            skLineSegment(sketch, "E81", {"start": v(-15, 108) * mm, "end": v(-15, 120) * mm});
            skLineSegment(sketch, "E82", {"start": v(15.03, 90) * mm, "end": v(15, 90.03) * mm});
            skLineSegment(sketch, "E83", {"start": v(15, 90.03) * mm, "end": v(15, 120) * mm});
            skArc(sketch, "E84", {"start": v(15, 120) * mm, "mid": v(0, 135) * mm, "end": v(-15, 120) * mm});
            skLineSegment(sketch, "E85", {"start": v(-80, 0) * mm, "end": v(80, 0) * mm, "construction": true});
            skLineSegment(sketch, "E86", {"start": v(-33, 90) * mm, "end": v(-15, 108) * mm});
            skLineSegment(sketch, "E87.MirrorCS", {"start": v(-15, -108) * mm, "end": v(-15, -120) * mm});
            skLineSegment(sketch, "E88.MirrorCS", {"start": v(15, -90.03) * mm, "end": v(15, -120) * mm});
            skArc(sketch, "E89.MirrorCS", {"start": v(15, -120) * mm, "mid": v(0, -135) * mm, "end": v(-15, -120) * mm});
            skCircle(sketch, "E90.MirrorC", {"center": v(0, -120) * mm, "radius": 6 * mm});
            skLineSegment(sketch, "E91.MirrorCS", {"start": v(15.03, -90) * mm, "end": v(15, -90.03) * mm});
            skLineSegment(sketch, "E92.MirrorCS", {"start": v(-33, -90) * mm, "end": v(-15, -108) * mm});
            skLineSegment(sketch, "E93.MirrorCS", {"start": v(0, -120) * mm, "end": v(0, -90) * mm, "construction": true});
            skSolve(sketch);
        }
        {
            var Q0;
            Q0=makeQuery(id+"F16.imprint","IMPRINT",FACE,{"disambiguationData":[TD([[makeQuery(id+"F16.imprint","IMPRINT",EDGE,{"derivedFrom":sQuery(id+"F16.wireOp",EDGE,"E88.MirrorCS")}),-1.0]])]});
            var Q1;
            Q1=makeQuery(id+"F16.imprint","IMPRINT",FACE,{"disambiguationData":[TD([[makeQuery(id+"F16.imprint","IMPRINT",EDGE,{"derivedFrom":makeQuery(id+"F1.opExtrude","CAP_EDGE",EDGE,{"disambiguationData":[OSD([sQuery(id+"F0.wireOp",EDGE,"E1.left")])],"isStart":true})}),-1.0]])]});
            var Q2;
            Q2=makeQuery(id+"F16.imprint","IMPRINT",FACE,{"disambiguationData":[TD([[makeQuery(id+"F16.imprint","IMPRINT",EDGE,{"derivedFrom":sQuery(id+"F16.wireOp",EDGE,"E79")}),-1.0]])]});
            var Q3;
            Q3=makeQuery(id+"F2.opExtrude","CAP_FACE",FACE,{"disambiguationData":[OSD([sQuery(id+"F0.wireOp",EDGE,"E12"),sQuery(id+"F0.wireOp",EDGE,"E13"),sQuery(id+"F0.wireOp",EDGE,"E14"),sQuery(id+"F0.wireOp",EDGE,"E15"),sQuery(id+"F0.wireOp",EDGE,"E17.filletArc"),sQuery(id+"F0.wireOp",EDGE,"E18.filletArc"),sQuery(id+"F0.wireOp",EDGE,"E19.filletArc"),sQuery(id+"F0.wireOp",EDGE,"E20.filletArc"),sQuery(id+"F0.wireOp",EDGE,"E25.0"),sQuery(id+"F0.wireOp",EDGE,"E25.1"),sQuery(id+"F0.wireOp",EDGE,"E25.2"),sQuery(id+"F0.wireOp",EDGE,"E25.3"),sQuery(id+"F0.wireOp",EDGE,"E25.4"),sQuery(id+"F0.wireOp",EDGE,"E25.5"),sQuery(id+"F0.wireOp",EDGE,"E25.6"),sQuery(id+"F0.wireOp",EDGE,"E25.7")])],"isStart":false});
            extrude(context, id + "F17", {"entities" : qUnion([Q0, Q1, Q2]), "operationType" : NewBodyOperationType.ADD, "endBound" : BoundingType.UP_TO_SURFACE, "endBoundEntityFace" : qUnion([Q3]), "depth" : 25 * mm});
        }
    });
